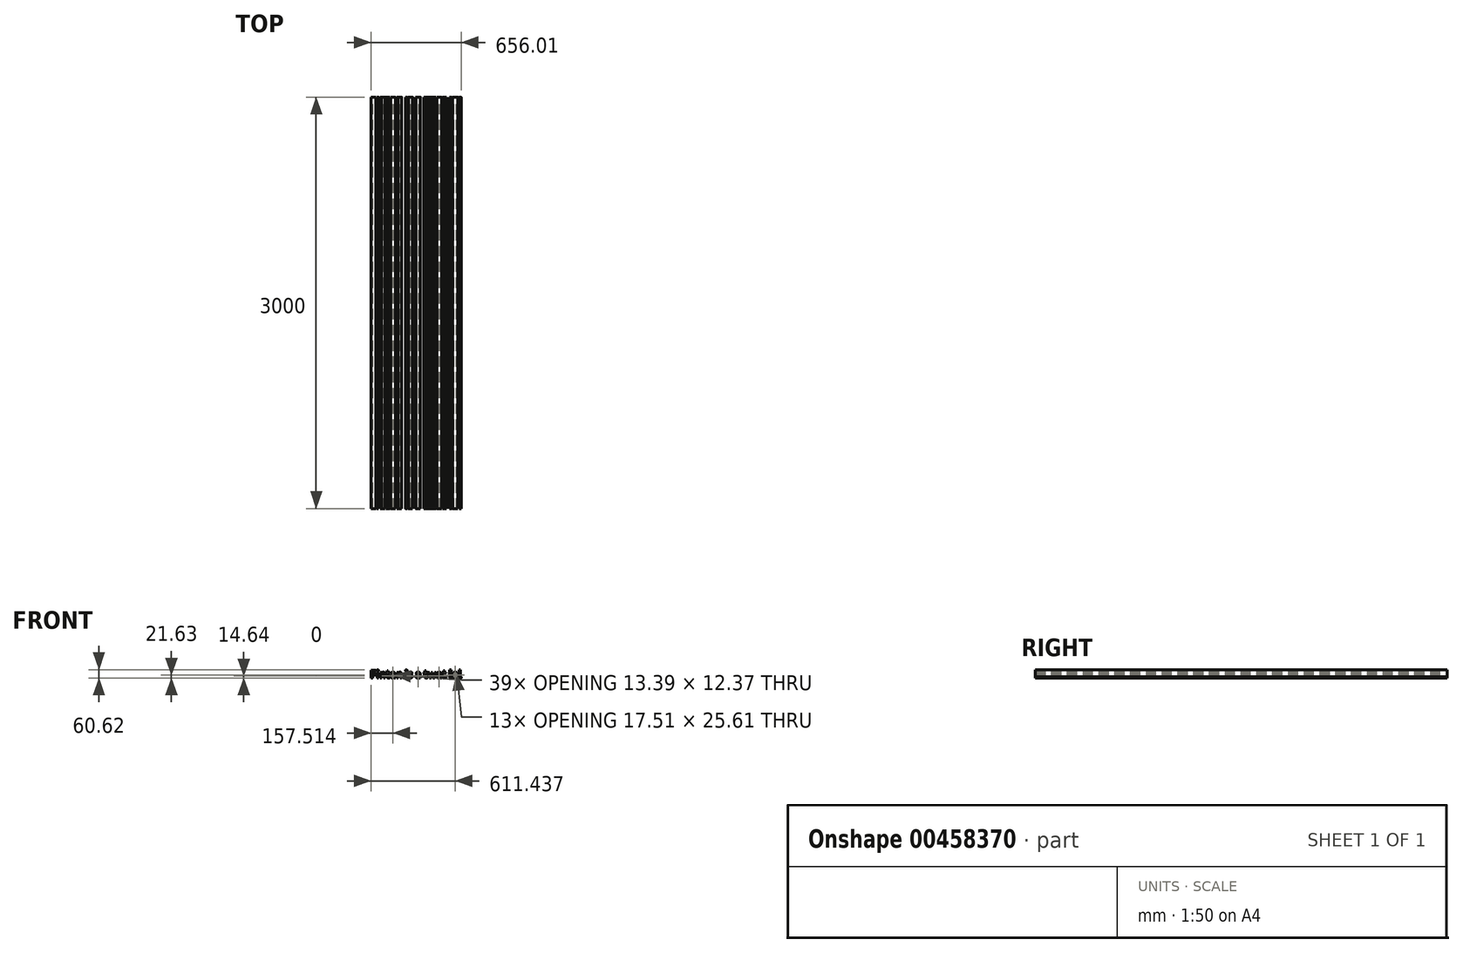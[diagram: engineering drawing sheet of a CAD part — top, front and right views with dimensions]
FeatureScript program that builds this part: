
annotation { "Feature Type Name" : "Feature", "Feature Type Description" : "" }
export const myFeature = defineFeature(function(context is Context, id is Id, definition is map)
    precondition{}
    {
        {
            var Q0;
            Q0=qCreatedBy(makeId("Front.planeOp"),FACE);
            var sketch = newSketch(context, id + "F0", { "sketchPlane" : qUnion([Q0])});
            skText(sketch, "E0", { "text": "Fintan is a twat lol", "fontName": "NotoSansCJKjp-Bold.otf"});
            const initialGuessF0  = {"E0": [-0.06219, -0.0053, 1, 0, 0.05297]};
            skSetInitialGuess(sketch, initialGuessF0);
            skSolve(sketch);
        }
        {
            var Q0;
            Q0 = qSketchRegion(id + "F0", true);
            extrude(context, id + "F1", {"entities" : qUnion([Q0]), "depth" : 3000 * mm, "offsetDistance" : 25 * mm});
        }
    });
